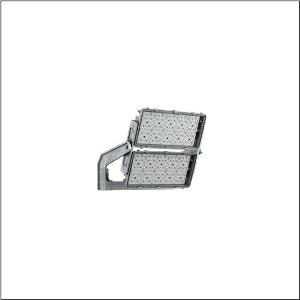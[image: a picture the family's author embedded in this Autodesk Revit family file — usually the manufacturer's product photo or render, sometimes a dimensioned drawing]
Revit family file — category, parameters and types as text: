
# Revit family: floodlight_fl_11_maxi_remote___rs07_5xa779514k01aa_47cf
name_source: partatom
category: Lighting Fixtures
units: mm (PartAtom-declared; Revit-internal decimal feet)

## family parameters
Cut with Voids When Loaded = No
Host = Face
Light Source = No
Part Type = Normal
Room Calculation Point = No
Round Connector Dimension = Use Diameter
Shared = No

## types (1)
- --- (1 x LED, 88570 lm, 916.8 W, 5700K)
    Apparent Load = 917 VA
    CIE Flux Codes = 80 93 99 100 99
    Color Rendering = 90
    Color Temperature = 5700K
    Default Elevation = 1800 mm
    Description = Floodlight FL 11  maxi  Remote floodlight; light control with lens of PMMA; cover panel of toughened safety glass, transparent; light distribution: RS07, rotationally symmetric direct distribution, LEDcolour temperature: 5700K, rated luminous flux: 88.570lm, colour rendering: CRI > 90, light colour: 957; luminous efficacy: 97lm/W; brightness control: DMX+RDM; with terminal, 6-pole, max. 2.5mm², mains connection: 220..240V/380..400V AC, 50/60Hz, surge voltage resistance: line to ground: 10kV, ECG replaceable separately, no afterglow with DALI off / DMX off command, LED unit replaceable without ESD environment, dustproof LED module, dimming range 10..100%; 917W floodlight with 2x LED unit of diecast aluminium, coated grey; length: 713mm / width: 651mm / height: 338mm; mounting bracket, of diecast aluminium, uncoated, natural, equipment: Power, protection rating (complete): IP66; insulation class (complete): insulation class I (protective earthing); certification: CE, ENEC, VDE; ball protection: ball impact resistance with accessories, impact resistance: IK07; rated ambient temperature 10°C, only for outdoor installations, permissible operating ambient temperature: -40..+30°C, permissible storage temperature: -40..+85°C; packaging unit: 1 piece

Light Distribution: RS07
    Height = 320 mm
    Lamp = 1 x LED
    Lamp Light Flux = 88570 lm
    Lamp Power = 916.8 W
    Lamp count = 1
    Length = 712 mm
    Luminous efficacy = 97 lm/W
    Manufacturer = Siteco
    ModVariant = No
    Model = 5XA779514K01AA
    Mounting Place = Ceiling
    Mounting Type = Surface mounted
    Number of Poles = 1
    OnlyDefault = Yes
    Power Factor = 1
    Product Name = Floodlight FL 11 maxi Remote | RS07
    Product group = floodlight | ceiling mounted
    ProductGroupID = 303
    Protection Class = Protection class I
    Protection Degree = IP 66
    RLX_Detail_Level = 1
    RLX_Emergency_Light_Flux = 0 lm
    RLX_Emergency_Type = 0
    RLX_Emergency_Type_DB = No
    RlxData = <blob elided: 41085 chars, md5=42141201>
    Socket = socket
    Standby Power = 0 W
    System Light Flux = 88570 lm
    System Power = 917 W
    Type Comments = factory setting: luminous flux: 100 % | dim-lin: 254 | 950 mA
    Type Image = l_1006788.jpg
    URL = http://relux.com
    VarID = @adj_132897
    Voltage = 0 V
    Weight = 0.00 kg
    Width = 655 mm

## geometry (parser evidence)
native form markers: Blend x4, Sweep x13
no freeform markers — native parametric forms only
